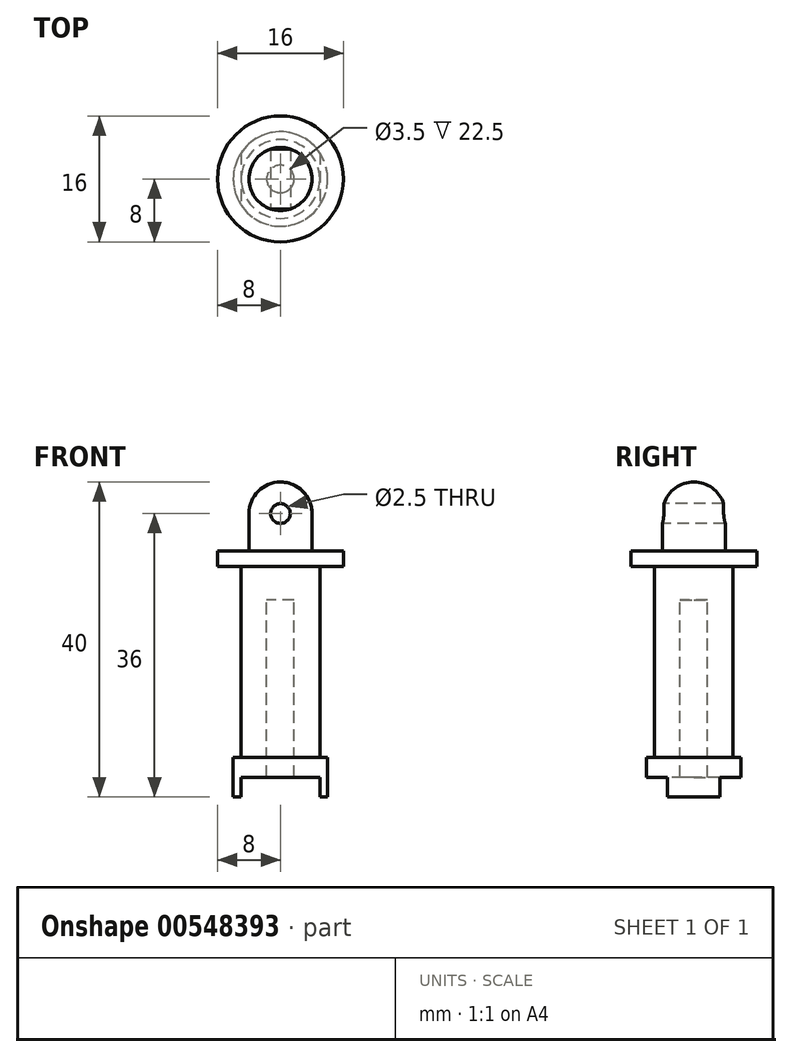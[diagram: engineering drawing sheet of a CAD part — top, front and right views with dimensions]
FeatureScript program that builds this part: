
annotation { "Feature Type Name" : "Feature", "Feature Type Description" : "" }
export const myFeature = defineFeature(function(context is Context, id is Id, definition is map)
    precondition{}
    {
        {
            var Q0;
            Q0=qCreatedBy(makeId("Front.planeOp"),FACE);
            var sketch = newSketch(context, id + "F0", { "sketchPlane" : qUnion([Q0])});
            skLineSegment(sketch, "E0", {"start": v(1.75, 0) * mm, "end": v(6, 0) * mm});
            skLineSegment(sketch, "E1", {"start": v(6, 0) * mm, "end": v(6, 5) * mm});
            skLineSegment(sketch, "E2", {"start": v(6, 5) * mm, "end": v(5, 5) * mm});
            skLineSegment(sketch, "E3", {"start": v(5, 5) * mm, "end": v(5, 29.25) * mm});
            skLineSegment(sketch, "E4", {"start": v(5, 29.25) * mm, "end": v(8, 29.25) * mm});
            skLineSegment(sketch, "E5", {"start": v(8, 29.25) * mm, "end": v(8, 31.25) * mm});
            skLineSegment(sketch, "E6", {"start": v(8, 31.25) * mm, "end": v(4, 31.25) * mm});
            skLineSegment(sketch, "E7", {"start": v(4, 31.25) * mm, "end": v(4, 36) * mm});
            skLineSegment(sketch, "E8", {"start": v(0, 40) * mm, "end": v(0, 40) * mm});
            skLineSegment(sketch, "E9", {"start": v(0, 40) * mm, "end": v(0, 25) * mm});
            skPoint(sketch, "E10.visualSharp", {"position": v(4, 40) * mm});
            skArc(sketch, "E10.filletArc", {"start": v(4, 36) * mm, "mid": v(2.83, 38.83) * mm, "end": v(0, 40) * mm});
            skLineSegment(sketch, "E11", {"start": v(0, 25) * mm, "end": v(1.75, 25) * mm});
            skLineSegment(sketch, "E12", {"start": v(1.75, 25) * mm, "end": v(1.75, 0) * mm});
            skSolve(sketch);
        }
        {
            var Q0;
            Q0 = qSketchRegion(id + "F0", true);
            var Q1;
            Q1=sQuery(id+"F0.wireOp",EDGE,"E9");
            revolve(context, id + "F1", {"entities" : qUnion([Q0]), "axis" : qUnion([Q1]), "revolveType" : RevolveType.FULL});
        }
        {
            var Q0;
            Q0=qCreatedBy(makeId("Front.planeOp"),FACE);
            var sketch = newSketch(context, id + "F2", { "sketchPlane" : qUnion([Q0])});
            skLineSegment(sketch, "E13.bottom", {"start": v(-5, 0) * mm, "end": v(5, 0) * mm});
            skLineSegment(sketch, "E13.top", {"start": v(-5, 2.5) * mm, "end": v(5, 2.5) * mm});
            skLineSegment(sketch, "E13.left", {"start": v(-5, 0) * mm, "end": v(-5, 2.5) * mm});
            skLineSegment(sketch, "E13.right", {"start": v(5, 0) * mm, "end": v(5, 2.5) * mm});
            skCircle(sketch, "E14", {"center": v(0, 36) * mm, "radius": 1.25 * mm});
            skSolve(sketch);
        }
        {
            var Q0;
            Q0 = qSketchRegion(id + "F2", true);
            extrude(context, id + "F3", {"entities" : qUnion([Q0]), "operationType" : NewBodyOperationType.REMOVE, "endBound" : BoundingType.SYMMETRIC, "oppositeDirection" : true, "depth" : 25 * mm, "offsetDistance" : 25 * mm});
        }
    });
